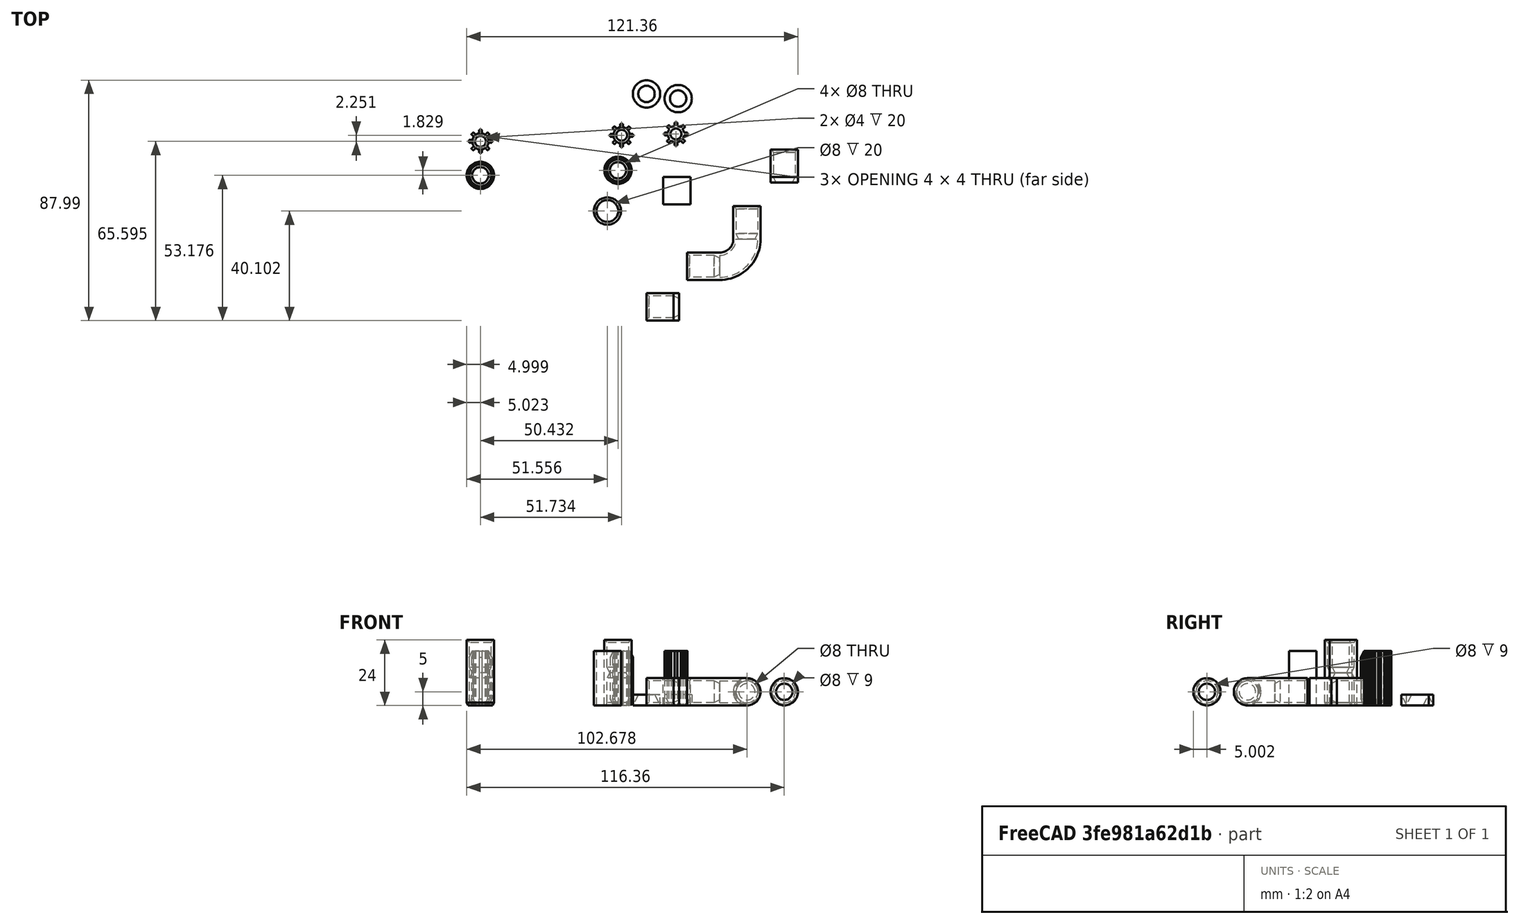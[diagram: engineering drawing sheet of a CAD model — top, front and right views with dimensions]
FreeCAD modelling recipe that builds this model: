
FCSTD DOCUMENT  (FreeCAD 0.20R29177 +426 (Git))
Label: JavaBase
License: All rights reserved
LicenseURL: http://en.wikipedia.org/wiki/All_rights_reserved
objects: Part::FeaturePython×25, Part::Cut×15, Part::Part2DObjectPython×12, App::DocumentObjectGroup×9, Part::Refine×4, Part::Feature×4, Part::Extrusion×4, Part::MultiFuse×3, Part::Cone×3, Part::Torus×2, Part::Box×1
note: 73 computed .brp shape members not serialized (recipe doc carries the construction recipe); baked Part::Feature solids carry a one-line shape summary decoded from their .brp

FEATURE [Part::Cut] Cut002005
  Placement = pos=(-51.1713,3.1e-15,0) rot=(0,0,1;0rad)
FEATURE [Part::Cut] Cut002027006
FEATURE [Part::Refine] Cut002027008001
FEATURE [Part::FeaturePython] Tube  # WARN: FeaturePython — macro-defined, semantics opaque (R4)
  AttacherType = Attacher::AttachEngine3D
  Height = 20
  InnerRadius = 4
  OuterRadius = 5
  Placement = pos=(-20.4335,-2.43824,-9e-16) rot=(0,0,1;0rad)
FEATURE [Part::Cut] Cut
  Base = -> Cut002027008001
  Tool = -> Cut002027006
FEATURE [Part::Feature] Face
  shape: bbox 8.4 x 8.4 x 2e-07 mm, 1 faces, 0 solids (baked)
FEATURE [Part::Extrusion] Extrusion
  Base = -> Face
  Dir = (0,0,-0.357849)
  DirMode = 0
  FaceMakerClass = Part::FaceMakerBullseye
  LengthFwd = 0
  LengthRev = 0
  Solid = true
  Symmetric = false
FEATURE [Part::Cut] Cut002027008002
  Base = -> Cut
  Placement = pos=(-116.451,-32.1684,-6) rot=(0,0,1;0rad)
  Tool = -> Extrusion
FEATURE [Part::Part2DObjectPython] Line001  # Draft 2D object (typed FeaturePython)
  Area = 0
  ChamferSize = 0
  Closed = false
  End = (0.313896,-3e-15,22)
  FilletRadius = 0
  Length = 9
  MakeFace = true
  Placement = pos=(0.313896,0,13) rot=(1,0,0;3.14159rad)
  Points = (2) [(0,0,0),(5.32907e-15,3e-15,-9)]
  Start = (0.313896,0,13)
  Subdivisions = 0
FEATURE [Part::Part2DObjectPython] Line002  # Draft 2D object (typed FeaturePython)
  Area = 0
  ChamferSize = 0
  Closed = false
  End = (0.313896,-2e-15,-2)
  FilletRadius = 0
  Length = 9
  MakeFace = true
  Placement = pos=(0.313896,1e-15,7) rot=(1,0,0;3.14159rad)
  Points = (2) [(0,0,0),(5.32907e-15,3e-15,9)]
  Start = (0.313896,1e-15,7)
  Subdivisions = 0
FEATURE [Part::Part2DObjectPython] Rectangle  # Draft 2D object (typed FeaturePython)
  Area = 550.412
  ChamferSize = 0
  Columns = 1
  FilletRadius = 0
  Height = 20.1253
  Length = 27.3493
  MakeFace = true
  Placement = pos=(-13.3608,10.0626,7) rot=(1,0,0;3.14159rad)
  Rows = 1
FEATURE [Part::Part2DObjectPython] Rectangle001  # Draft 2D object (typed FeaturePython)
  Area = 767.456
  ChamferSize = 0
  Columns = 1
  FilletRadius = 0
  Height = 30.1071
  Length = 25.4909
  MakeFace = true
  Placement = pos=(-12.4315,15.0535,13) rot=(1,0,0;3.14159rad)
  Rows = 1
FEATURE [Part::FeaturePython] Slice  # WARN: FeaturePython — macro-defined, semantics opaque (R4)
  Base = -> Cut002005
  Mode = 1
  Tolerance = 0
  Tools = -> [Rectangle001]
FEATURE [Part::FeaturePython] Slice_child0  label="Slice.0"  # WARN: FeaturePython — macro-defined, semantics opaque (R4)
  Base = -> Slice
  FilterType = 1
  Invert = false
  OverrideMaxVal = 0
  Placement = pos=(0,0,1) rot=(0,0,1;0rad)
  WindowFrom = 80
  WindowTo = 100
  items = 0
FEATURE [Part::FeaturePython] Slice_child1  label="Slice.1"  # WARN: FeaturePython — macro-defined, semantics opaque (R4)
  Base = -> Slice
  FilterType = 1
  Invert = false
  OverrideMaxVal = 0
  WindowFrom = 80
  WindowTo = 100
  items = 1
FEATURE [App::DocumentObjectGroup] GrExplode_Slice  label="Exploded Slice"
  Group = -> [Slice_child1]
FEATURE [Part::FeaturePython] Slice001  # WARN: FeaturePython — macro-defined, semantics opaque (R4)
  Base = -> Slice_child1
  Mode = 1
  Tolerance = 0
  Tools = -> [Rectangle]
FEATURE [Part::FeaturePython] Slice001_child0  label="Slice001.0"  # WARN: FeaturePython — macro-defined, semantics opaque (R4)
  Base = -> Slice001
  FilterType = 1
  Invert = false
  OverrideMaxVal = 0
  WindowFrom = 80
  WindowTo = 100
  items = 0
FEATURE [Part::FeaturePython] Slice001_child1  label="Slice001.1"  # WARN: FeaturePython — macro-defined, semantics opaque (R4)
  Base = -> Slice001
  FilterType = 1
  Invert = false
  OverrideMaxVal = 0
  Placement = pos=(1.8e-15,-1e-15,-3) rot=(0,0,1;0rad)
  WindowFrom = 80
  WindowTo = 100
  items = 1
FEATURE [Part::Part2DObjectPython] Rectangle002  # Draft 2D object (typed FeaturePython)
  Area = 660.767
  ChamferSize = 0
  Columns = 1
  FilletRadius = 0
  Height = 24.9261
  Length = 26.5091
  MakeFace = true
  Placement = pos=(-13.9406,12.463,9) rot=(1,0,0;3.14159rad)
  Rows = 1
FEATURE [Part::Part2DObjectPython] Rectangle003  # Draft 2D object (typed FeaturePython)
  Area = 801.11
  ChamferSize = 0
  Columns = 1
  FilletRadius = 0
  Height = 25.9621
  Length = 30.8569
  MakeFace = true
  Placement = pos=(-16.1146,12.9811,11) rot=(1,0,0;3.14159rad)
  Rows = 1
FEATURE [Part::FeaturePython] Slice002  # WARN: FeaturePython — macro-defined, semantics opaque (R4)
  Base = -> Slice001_child0
  Mode = 1
  Tolerance = 0
  Tools = -> [Rectangle003]
FEATURE [Part::FeaturePython] Slice002_child0  label="Slice002.0"  # WARN: FeaturePython — macro-defined, semantics opaque (R4)
  Base = -> Slice002
  FilterType = 1
  Invert = false
  OverrideMaxVal = 0
  WindowFrom = 80
  WindowTo = 100
  items = 0
FEATURE [App::DocumentObjectGroup] GrExplode_Slice002  label="Exploded Slice002"
  Group = -> [Slice002_child0]
FEATURE [Part::FeaturePython] Slice002_child1  label="Slice002.1"  # WARN: FeaturePython — macro-defined, semantics opaque (R4)
  Base = -> Slice002
  FilterType = 1
  Invert = false
  OverrideMaxVal = 0
  Placement = pos=(0,0,-2) rot=(0,0,1;0rad)
  WindowFrom = 80
  WindowTo = 100
  items = 1
FEATURE [Part::FeaturePython] Slice003  # WARN: FeaturePython — macro-defined, semantics opaque (R4)
  Base = -> Slice002_child0
  Mode = 1
  Tolerance = 0
  Tools = -> [Rectangle002]
FEATURE [App::DocumentObjectGroup] GrExplode_Slice003  label="Exploded Slice003"
FEATURE [Part::FeaturePython] Slice003_child0  label="Slice003.0"  # WARN: FeaturePython — macro-defined, semantics opaque (R4)
  Base = -> Slice003
  FilterType = 1
  Invert = false
  OverrideMaxVal = 0
  WindowFrom = 80
  WindowTo = 100
  items = 0
FEATURE [Part::Feature] Face001
  shape: bbox 10 x 10 x 2e-07 mm, 1 faces, 0 solids (baked)
FEATURE [Part::Extrusion] Extrusion001
  Base = -> Face001
  Dir = (0,0,-3)
  DirMode = 0
  FaceMakerClass = Part::FaceMakerBullseye
  LengthFwd = 0
  LengthRev = 0
  Solid = true
  Symmetric = false
FEATURE [Part::Feature] Face002
  Placement = pos=(1.8e-15,-1e-15,3) rot=(0,0,1;0rad)
  shape: bbox 10 x 10 x 2e-07 mm, 1 faces, 0 solids (baked)
FEATURE [Part::Extrusion] Extrusion002
  Base = -> Face002
  Dir = (0,0,-3)
  DirMode = 0
  FaceMakerClass = Part::FaceMakerBullseye
  LengthFwd = 0
  LengthRev = 0
  Placement = pos=(-1.8e-15,1e-15,-2) rot=(0,0,1;0rad)
  Solid = true
  Symmetric = false
FEATURE [Part::MultiFuse] Fusion
  Placement = pos=(-9.48569,-0.0305466,3) rot=(0,0,1;0rad)
  Shapes = -> [Slice_child0,Extrusion002,Slice002_child1,Slice003_child0,Extrusion001,Slice001_child1]
FEATURE [App::DocumentObjectGroup] GrExplode_Slice001  label="Exploded Slice001"
  Group = -> [Slice001_child0,Fusion]
FEATURE [Part::Part2DObjectPython] Rectangle004  # Draft 2D object (typed FeaturePython)
  Area = 333.125
  ChamferSize = 0
  Columns = 1
  FilletRadius = 0
  Height = 16.6562
  Length = 20
  MakeFace = true
  Placement = pos=(-19.1718,8.29757,10) rot=(1,0,0;3.14159rad)
  Rows = 1
FEATURE [Part::Part2DObjectPython] Rectangle005  # Draft 2D object (typed FeaturePython)
  Area = 1117.96
  ChamferSize = 0
  Columns = 1
  FilletRadius = 0
  Height = 26.2818
  Length = 42.5375
  MakeFace = true
  Placement = pos=(-30.4405,13.1103,14) rot=(1,0,0;3.14159rad)
  Rows = 1
FEATURE [Part::FeaturePython] Slice004  # WARN: FeaturePython — macro-defined, semantics opaque (R4)
  Base = -> Fusion
  Mode = 1
  Tolerance = 0
  Tools = -> [Rectangle005]
FEATURE [Part::FeaturePython] Slice004_child0  label="Slice004.0"  # WARN: FeaturePython — macro-defined, semantics opaque (R4)
  Base = -> Slice004
  FilterType = 1
  Invert = false
  OverrideMaxVal = 0
  WindowFrom = 80
  WindowTo = 100
  items = 0
FEATURE [Part::FeaturePython] Slice004_child1  label="Slice004.1"  # WARN: FeaturePython — macro-defined, semantics opaque (R4)
  Base = -> Slice004
  FilterType = 1
  Invert = false
  OverrideMaxVal = 0
  WindowFrom = 80
  WindowTo = 100
  items = 1
FEATURE [App::DocumentObjectGroup] GrExplode_Slice004  label="Exploded Slice004"
  Group = -> [Slice004_child1]
FEATURE [Part::FeaturePython] Slice005  # WARN: FeaturePython — macro-defined, semantics opaque (R4)
  Base = -> Slice004_child1
  Mode = 1
  Tolerance = 0
  Tools = -> [Rectangle004]
FEATURE [Part::FeaturePython] Slice005_child0  label="Slice005.0"  # WARN: FeaturePython — macro-defined, semantics opaque (R4)
  Base = -> Slice005
  FilterType = 1
  Invert = false
  OverrideMaxVal = 0
  WindowFrom = 80
  WindowTo = 100
  items = 0
FEATURE [Part::FeaturePython] Slice005_child1  label="Slice005.1"  # WARN: FeaturePython — macro-defined, semantics opaque (R4)
  Base = -> Slice005
  FilterType = 1
  Invert = false
  OverrideMaxVal = 0
  WindowFrom = 80
  WindowTo = 100
  items = 1
FEATURE [Part::Cone] Cone
  Angle = 360
  AttacherType = Attacher::AttachEngine3D
  Height = 4
  Placement = pos=(-14.7012,36.9584,-3.6e-15) rot=(0,0,1;0rad)
  Radius1 = 3
  Radius2 = 5
FEATURE [Part::Feature] Face003
  Placement = pos=(-1.52941,36.989,-12) rot=(0,0,1;0rad)
  shape: bbox 10 x 10 x 2e-07 mm, 1 faces, 0 solids (baked)
FEATURE [Part::Part2DObjectPython] Circle  # Draft 2D object (typed FeaturePython)
  Area = 78.5398
  FirstAngle = 0
  LastAngle = 0
  MakeFace = true
  Placement = pos=(-14.7012,36.9584,4) rot=(0,0,1;0rad)
  Radius = 5
FEATURE [Part::Extrusion] Extrusion003
  Base = -> Circle
  Dir = (0,0,-4)
  DirMode = 0
  FaceMakerClass = Part::FaceMakerBullseye
  LengthFwd = 0
  LengthRev = 0
  Solid = true
  Symmetric = false
FEATURE [Part::Cut] Cut002027008003
  Base = -> Extrusion003
  Placement = pos=(9.5838,-12.2271,3.6e-15) rot=(0,0,1;0rad)
  Tool = -> Cone
FEATURE [Part::Cut] Cut002027008004
  Base = -> Extrusion003
  Placement = pos=(8.58889,77.4078,4) rot=(-1,0,0;3.14159rad)
  Tool = -> Cone
FEATURE [Part::Box] Box  label="Cube"
  AttacherType = Attacher::AttachEngine3D
  Height = 10
  Length = 10
  Width = 10
FEATURE [Part::MultiFuse] Fusion001
  Shapes = -> [Slice004_child0,Slice005_child0,Slice005_child1]
FEATURE [App::DocumentObjectGroup] GrExplode_Slice005  label="Exploded Slice005"
  Group = -> [Fusion001]
FEATURE [Part::Refine] Fusion001001
  Placement = pos=(-53.8195,10.667,0) rot=(0,0,1;0rad)
  Source = -> Fusion001
FEATURE [Part::Cut] Cut002027008005
  Base = -> Cut
  Placement = pos=(-106.662,-31.1327,-6) rot=(0,0,1;0rad)
  Tool = -> Extrusion
FEATURE [Part::Cut] Cut002027008006
  Base = -> Extrusion003
  Placement = pos=(20.1788,1.77384,4e-15) rot=(0,0,1;0rad)
  Tool = -> Cone
FEATURE [Part::Cut] Cut002027008007
  Base = -> Extrusion003
  Placement = pos=(9.5838,61.6898,20) rot=(1,0,0;3.14159rad)
  Tool = -> Cone
FEATURE [Part::Cut] Cut002027008008
  Base = -> Cut002027008002
  Tool = -> Cut002027008007
FEATURE [Part::Cut] Cut002027008009
  Base = -> Cut002027008008
  Placement = pos=(-10.1159,0.574683,2.7e-15) rot=(0,0,1;0rad)
  Tool = -> Cut002027008003
FEATURE [Part::Cut] Cut002027008010
  Base = -> Cut002027008008
  Placement = pos=(-61.8496,-1.67613,0) rot=(0,0,1;0rad)
  Tool = -> Cut002027008003
FEATURE [Part::Refine] Fusion001002
  Placement = pos=(-3.38776,12.4959,0) rot=(0,0,1;0rad)
  Source = -> Fusion001
FEATURE [Part::Cone] Cone001
  Angle = 360
  AttacherType = Attacher::AttachEngine3D
  Height = 1
  Placement = pos=(-57.3172,27.2145,-1) rot=(0,0,1;0rad)
  Radius1 = 4.5
  Radius2 = 5
FEATURE [Part::Cone] Cone002
  Angle = 360
  AttacherType = Attacher::AttachEngine3D
  Height = 1
  Placement = pos=(-57.3172,27.2145,-1) rot=(0,0,1;0rad)
  Radius1 = 6.5
  Radius2 = 7
FEATURE [Part::Cut] Cut002027008011
  Base = -> Cone002
  Placement = pos=(-9.67415,-16.578,1) rot=(0,0,1;0rad)
  Tool = -> Cone001
FEATURE [Part::Cut] Cut002027008012
  Base = -> Fusion001001
  Tool = -> Cut002027008011
FEATURE [Part::Torus] Torus
  Angle1 = -180
  Angle2 = 180
  Angle3 = -90
  AttacherType = Attacher::AttachEngine3D
  Placement = pos=(20.6876,-12.6863,5) rot=(0,0,1;0rad)
  Radius1 = 10
  Radius2 = 5
  expr: Angle3 = -90°
FEATURE [Part::Refine] Fusion001003
  Placement = pos=(20.6876,-22.6558,18.1718) rot=(0,-1,0;1.5708rad)
  Source = -> Fusion001
FEATURE [Part::Part2DObjectPython] Rectangle006  # Draft 2D object (typed FeaturePython)
  Area = 1239.83
  ChamferSize = 0
  Columns = 1
  FilletRadius = 0
  Height = 29.2988
  Length = 42.3167
  MakeFace = true
  Placement = pos=(8.68764,-1.52799,-6.6494) rot=(0.57735,-0.57735,-0.57735;2.0944rad)
  Rows = 1
FEATURE [Part::FeaturePython] Slice006  # WARN: FeaturePython — macro-defined, semantics opaque (R4)
  Base = -> Fusion001003
  Mode = 1
  Tolerance = 0
  Tools = -> [Rectangle006]
FEATURE [Part::FeaturePython] Slice006_child0  label="Slice006.0"  # WARN: FeaturePython — macro-defined, semantics opaque (R4)
  Base = -> Slice006
  FilterType = 1
  Invert = false
  OverrideMaxVal = 0
  Placement = pos=(-2.84767,-14.8521,-3.6e-15) rot=(0,0,1;0rad)
  WindowFrom = 80
  WindowTo = 100
  items = 0
FEATURE [Part::FeaturePython] Slice006_child1  label="Slice006.1"  # WARN: FeaturePython — macro-defined, semantics opaque (R4)
  Base = -> Slice006
  FilterType = 1
  Invert = false
  OverrideMaxVal = 0
  Placement = pos=(21.684,-0.630213,-3.6e-15) rot=(0,0,1;1.5708rad)
  WindowFrom = 80
  WindowTo = 100
  items = 1
FEATURE [App::DocumentObjectGroup] GrExplode_Slice006  label="Exploded Slice006"
  Group = -> [Slice006_child0,Slice006_child1]
FEATURE [Part::Torus] Torus001
  Angle1 = -180
  Angle2 = 180
  Angle3 = -90
  AttacherType = Attacher::AttachEngine3D
  Placement = pos=(20.6876,-12.6863,5) rot=(0,0,1;0rad)
  Radius1 = 10
  Radius2 = 4
  expr: Angle3 = -90°
FEATURE [Part::Cut] Cut002027008013
  Base = -> Torus
  Tool = -> Torus001
FEATURE [Part::FeaturePython] Slice006_child002  label="Slice006.002"  # WARN: FeaturePython — macro-defined, semantics opaque (R4)
  Base = -> Slice006
  FilterType = 1
  Invert = false
  OverrideMaxVal = 0
  Placement = pos=(12,0,-3.6e-15) rot=(0,0,1;0rad)
  WindowFrom = 80
  WindowTo = 100
  items = 0
FEATURE [Part::FeaturePython] Slice006_child003  label="Slice006.003"  # WARN: FeaturePython — macro-defined, semantics opaque (R4)
  Base = -> Slice006
  FilterType = 1
  Invert = false
  OverrideMaxVal = 0
  Placement = pos=(8.0013,-21.374,-3.6e-15) rot=(0,0,1;1.5708rad)
  WindowFrom = 80
  WindowTo = 100
  items = 1
FEATURE [Part::Part2DObjectPython] Rectangle007  # Draft 2D object (typed FeaturePython)
  Area = 703.724
  ChamferSize = 0
  Columns = 1
  FilletRadius = 0
  Height = 23.3647
  Length = 30.1191
  MakeFace = true
  Placement = pos=(29.3107,10.0574,-2.68235) rot=(1,0,0;1.5708rad)
  Rows = 1
FEATURE [Part::FeaturePython] Slice007  # WARN: FeaturePython — macro-defined, semantics opaque (R4)
  Base = -> Slice006_child1
  Mode = 1
  Tolerance = 0
  Tools = -> [Rectangle007]
FEATURE [App::DocumentObjectGroup] GrExplode_Slice007  label="Exploded Slice007"
FEATURE [Part::Part2DObjectPython] Rectangle008  # Draft 2D object (typed FeaturePython)
  Area = 1117.47
  ChamferSize = 0
  Columns = 1
  FilletRadius = 0
  Height = 36.9314
  Length = 30.258
  MakeFace = true
  Placement = pos=(3.83996,-52.6675,-9.46569) rot=(0.57735,0.57735,0.57735;2.0944rad)
  Rows = 1
FEATURE [Part::FeaturePython] Slice008  # WARN: FeaturePython — macro-defined, semantics opaque (R4)
  Base = -> Slice006_child0
  Mode = 1
  Tolerance = 0
  Tools = -> [Rectangle008]
FEATURE [App::DocumentObjectGroup] GrExplode_Slice008  label="Exploded Slice008"
FEATURE [Part::MultiFuse] Fusion001004
  Shapes = -> [Slice006_child002,Cut002027008013,Slice006_child003]
